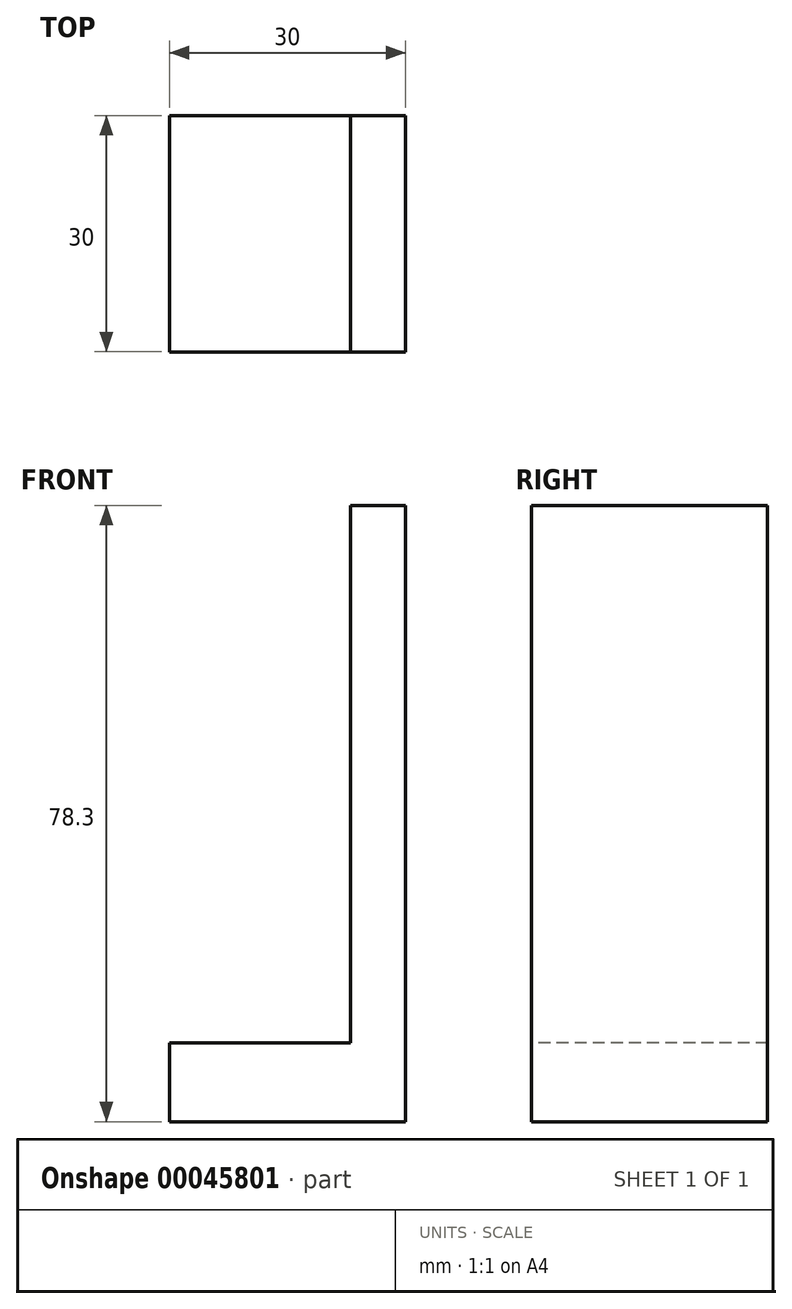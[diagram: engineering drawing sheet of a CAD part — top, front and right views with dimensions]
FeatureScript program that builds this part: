
annotation { "Feature Type Name" : "Feature", "Feature Type Description" : "" }
export const myFeature = defineFeature(function(context is Context, id is Id, definition is map)
    precondition{}
    {
        {
            var Q0;
            Q0=qCreatedBy(makeId("Top.planeOp"),FACE);
            var sketch = newSketch(context, id + "F0", { "sketchPlane" : qUnion([Q0])});
            skLineSegment(sketch, "E0.bottom", {"start": v(-15.62, 14.76) * mm, "end": v(14.38, 14.76) * mm});
            skLineSegment(sketch, "E0.top", {"start": v(-15.62, -15.24) * mm, "end": v(14.38, -15.24) * mm});
            skLineSegment(sketch, "E0.left", {"start": v(-15.62, 14.76) * mm, "end": v(-15.62, -15.24) * mm});
            skLineSegment(sketch, "E0.right", {"start": v(14.38, 14.76) * mm, "end": v(14.38, -15.24) * mm});
            skLineSegment(sketch, "E1", {"start": v(0, 68.81) * mm, "end": v(0, -51.14) * mm, "construction": true});
            skLineSegment(sketch, "E2", {"start": v(-58.6, 0) * mm, "end": v(54.63, 0) * mm, "construction": true});
            skSolve(sketch);
        }
        {
            var Q0;
            Q0 = qSketchRegion(id + "F0", true);
            extrude(context, id + "F1", {"entities" : qUnion([Q0]), "depth" : 10 * mm});
        }
        {
            var Q0;
            Q0=makeQuery(id+"F1.opExtrude","CAP_FACE",FACE,{"disambiguationData":[OSD([sQuery(id+"F0.wireOp",EDGE,"E0.bottom"),sQuery(id+"F0.wireOp",EDGE,"E0.top"),sQuery(id+"F0.wireOp",EDGE,"E0.left"),sQuery(id+"F0.wireOp",EDGE,"E0.right")])],"isStart":false});
            var sketch = newSketch(context, id + "F2", { "sketchPlane" : qUnion([Q0])});
            skLineSegment(sketch, "E3.bottom", {"start": v(14.38, 14.76) * mm, "end": v(7.38, 14.76) * mm});
            skLineSegment(sketch, "E3.top", {"start": v(14.38, -15.24) * mm, "end": v(7.38, -15.24) * mm});
            skLineSegment(sketch, "E3.left", {"start": v(14.38, 14.76) * mm, "end": v(14.38, -15.24) * mm});
            skLineSegment(sketch, "E3.right", {"start": v(7.38, 14.76) * mm, "end": v(7.38, -15.24) * mm});
            skSolve(sketch);
        }
        {
            var Q0;
            Q0=makeQuery(id+"F2.imprint","IMPRINT",FACE,{"disambiguationData":[TD([[makeQuery(id+"F2.imprint","IMPRINT",EDGE,{"derivedFrom":sQuery(id+"F2.wireOp",EDGE,"E3.bottom")}),-1.0]])]});
            extrude(context, id + "F3", {"entities" : qUnion([Q0]), "operationType" : NewBodyOperationType.ADD, "depth" : 68.3 * mm});
        }
    });
